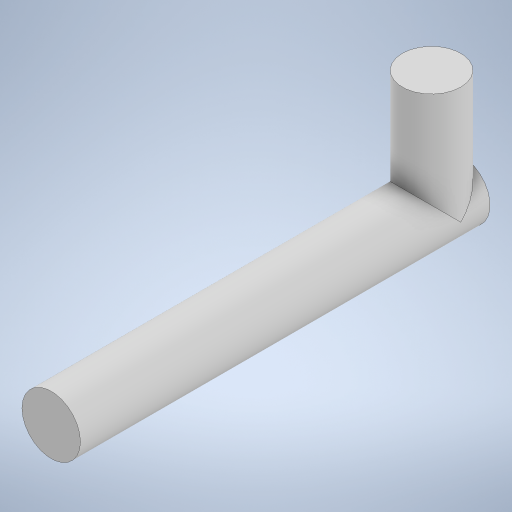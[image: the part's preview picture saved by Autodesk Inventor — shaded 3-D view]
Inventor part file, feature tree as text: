
AUTODESK INVENTOR PART (.ipt)
format: ipt  version: 2023 (Build 270158000, 158)  size: 230,912 bytes
history: native  units: in
note: dims shown in document units (in); Inventor stores cm internally (conversion verified against a paired STEP export)
features: extrude x2, sketch x2
ambient origin geometry x8: Origin, YZ Plane, XZ Plane, XY Plane, X Axis, Y Axis, Z Axis, Center Point
bodies: Solid1 (feature_tree)
feature tree (4):
  extrude  "Extrusion1"  Depth=1.6535in TaperAngle=0.0deg
  extrude  "Extrusion2"  Depth=0.1181in
  sketch  "Sketch1"  dims[d0=0.2362in d1=1.6535in d2=0.0in]
  sketch  "Sketch2"  dims[d3=0.1181in d4=0.2362in d5=0.4724in d6=0.0in]
